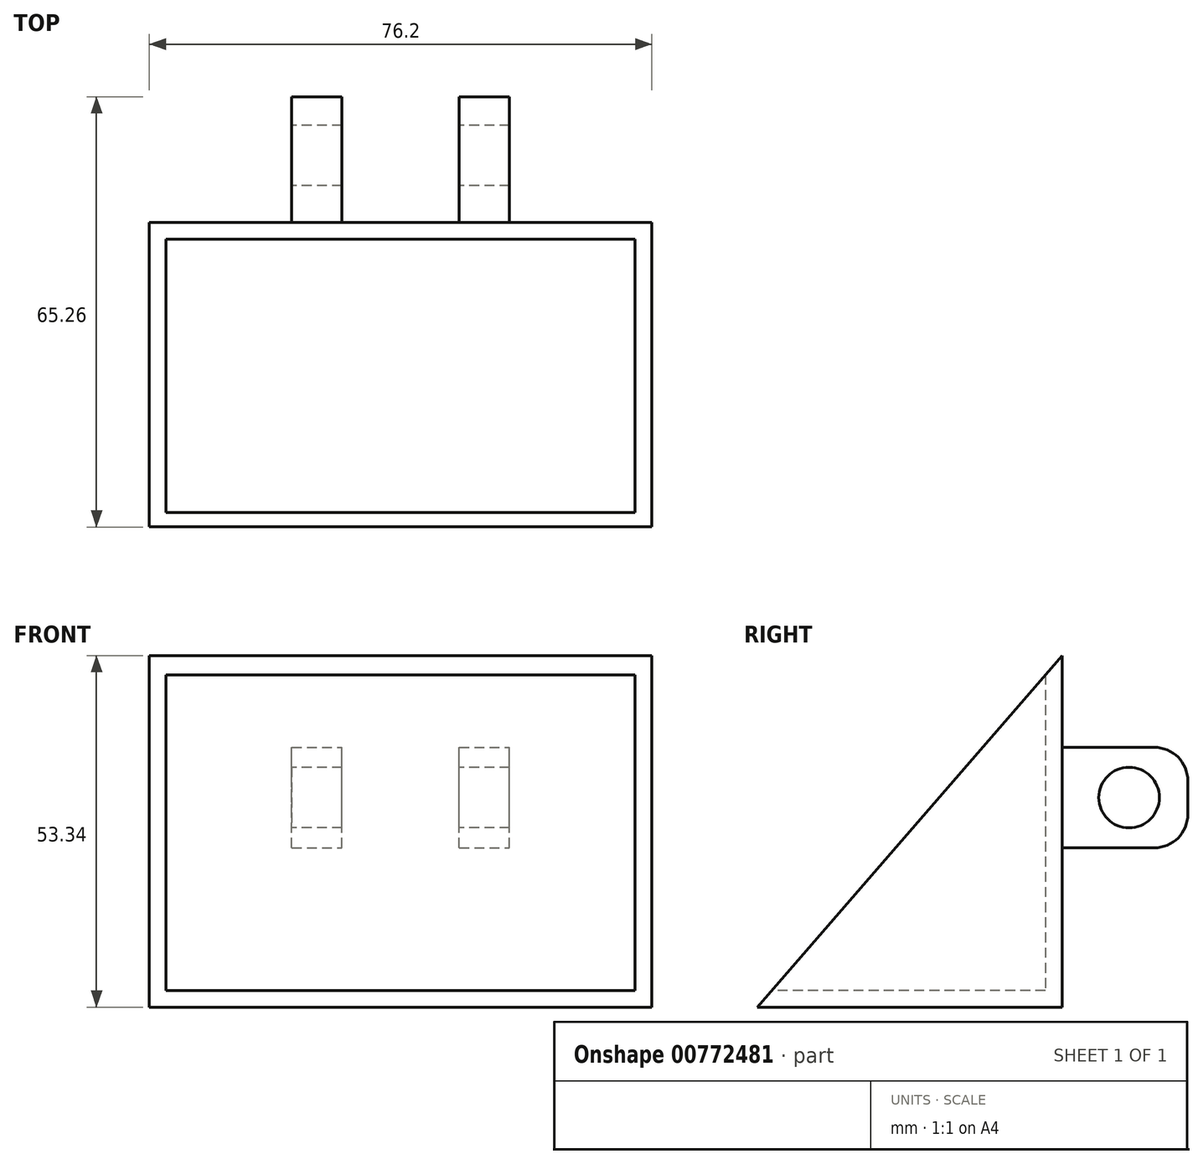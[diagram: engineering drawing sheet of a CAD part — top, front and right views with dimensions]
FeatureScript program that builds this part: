
annotation { "Feature Type Name" : "Feature", "Feature Type Description" : "" }
export const myFeature = defineFeature(function(context is Context, id is Id, definition is map)
    precondition{}
    {
        {
            var Q0;
            Q0=qCreatedBy(makeId("Right.planeOp"),FACE);
            var sketch = newSketch(context, id + "F0", { "sketchPlane" : qUnion([Q0])});
            skLineSegment(sketch, "E0", {"start": v(37.68, 21.55) * mm, "end": v(37.68, -31.79) * mm});
            skLineSegment(sketch, "E1", {"start": v(37.68, -31.79) * mm, "end": v(-8.53, -31.79) * mm});
            skLineSegment(sketch, "E2", {"start": v(-8.53, -31.79) * mm, "end": v(37.68, 21.55) * mm});
            skSolve(sketch);
        }
        {
            var Q0;
            Q0 = qSketchRegion(id + "F0", true);
            extrude(context, id + "F1", {"entities" : qUnion([Q0]), "endBound" : BoundingType.SYMMETRIC, "depth" : 76.2 * mm, "offsetDistance" : 25.4 * mm});
        }
        {
            var Q0;
            Q0=makeQuery(id+"F1.opExtrude","SWEPT_FACE",FACE,{"disambiguationData":[OSD([sQuery(id+"F0.wireOp",EDGE,"E2")])]});
            shell(context, id + "F2", {"entities" : qUnion([Q0]), "thickness" : 2.54 * mm});
        }
        {
            var Q0;
            Q0=makeQuery(id+"F1.opExtrude","SWEPT_FACE",FACE,{"disambiguationData":[OSD([sQuery(id+"F0.wireOp",EDGE,"E0")])]});
            var sketch = newSketch(context, id + "F3", { "sketchPlane" : qUnion([Q0])});
            skLineSegment(sketch, "E3.bottom", {"start": v(-8.9, -7.62) * mm, "end": v(-16.51, -7.62) * mm});
            skLineSegment(sketch, "E3.top", {"start": v(-8.9, 7.62) * mm, "end": v(-16.51, 7.62) * mm});
            skLineSegment(sketch, "E3.left", {"start": v(-8.9, -7.62) * mm, "end": v(-8.9, 7.62) * mm});
            skLineSegment(sketch, "E3.right", {"start": v(-16.51, -7.62) * mm, "end": v(-16.51, 7.62) * mm});
            skPoint(sketch, "E3.middle", {"position": v(-12.7, 0) * mm});
            skLineSegment(sketch, "E4.bottom", {"start": v(16.51, -7.62) * mm, "end": v(8.89, -7.62) * mm});
            skLineSegment(sketch, "E4.top", {"start": v(16.51, 7.62) * mm, "end": v(8.9, 7.62) * mm});
            skLineSegment(sketch, "E4.left", {"start": v(16.51, -7.62) * mm, "end": v(16.51, 7.62) * mm});
            skLineSegment(sketch, "E4.right", {"start": v(8.89, -7.62) * mm, "end": v(8.89, 7.62) * mm});
            skPoint(sketch, "E4.middle", {"position": v(12.7, 0) * mm});
            skSolve(sketch);
        }
        {
            var Q0;
            Q0 = qSketchRegion(id + "F3", true);
            extrude(context, id + "F4", {"entities" : qUnion([Q0]), "operationType" : NewBodyOperationType.ADD, "depth" : 19.05 * mm, "offsetDistance" : 25.4 * mm});
        }
        {
            var Q0;
            Q0=makeQuery(id+"F4.opExtrude","CAP_EDGE",EDGE,{"disambiguationData":[OSD([sQuery(id+"F3.wireOp",EDGE,"E3.top")])],"isStart":false});
            var Q1;
            Q1=makeQuery(id+"F4.opExtrude","CAP_EDGE",EDGE,{"disambiguationData":[OSD([sQuery(id+"F3.wireOp",EDGE,"E3.bottom")])],"isStart":false});
            var Q2;
            Q2=makeQuery(id+"F4.opExtrude","CAP_EDGE",EDGE,{"disambiguationData":[OSD([sQuery(id+"F3.wireOp",EDGE,"E4.bottom")])],"isStart":false});
            var Q3;
            Q3=makeQuery(id+"F4.opExtrude","CAP_EDGE",EDGE,{"disambiguationData":[OSD([sQuery(id+"F3.wireOp",EDGE,"E4.top")])],"isStart":false});
            fillet(context, id + "F5", {"entities" : qUnion([Q0, Q1, Q2, Q3]), "radius" : 5.08 * mm, "tangentPropagation" : true, "allowEdgeOverflow" : false});
        }
        {
            var Q0;
            Q0=makeQuery(id+"F4.opExtrude","SWEPT_FACE",FACE,{"disambiguationData":[OSD([sQuery(id+"F3.wireOp",EDGE,"E4.left")])]});
            var sketch = newSketch(context, id + "F6", { "sketchPlane" : qUnion([Q0])});
            skCircle(sketch, "E5", {"center": v(-47.82, 0) * mm, "radius": 4.6 * mm});
            skSolve(sketch);
        }
        {
            var Q0;
            Q0=makeQuery(id+"F6.imprint","IMPRINT",FACE,{"disambiguationData":[TD([[makeQuery(id+"F6.imprint","IMPRINT",EDGE,{"derivedFrom":sQuery(id+"F6.wireOp",EDGE,"E5")}),1.0]])]});
            extrude(context, id + "F7", {"entities" : qUnion([Q0]), "operationType" : NewBodyOperationType.REMOVE, "oppositeDirection" : true, "depth" : 39.88 * mm, "offsetDistance" : 25.4 * mm});
        }
    });
